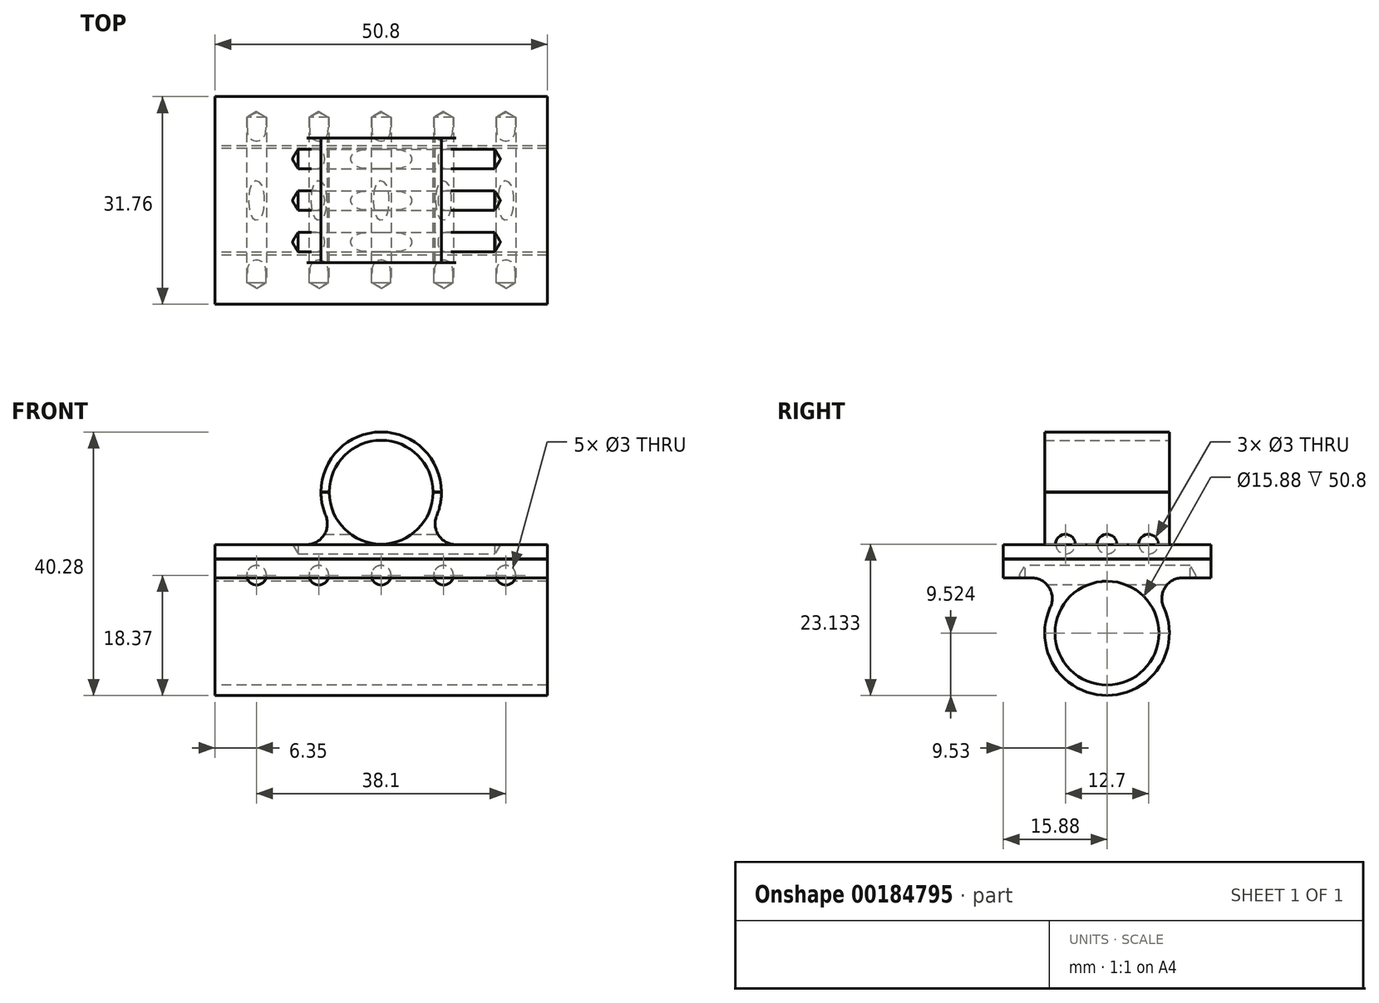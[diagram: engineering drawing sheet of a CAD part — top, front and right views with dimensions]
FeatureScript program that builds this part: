
annotation { "Feature Type Name" : "Feature", "Feature Type Description" : "" }
export const myFeature = defineFeature(function(context is Context, id is Id, definition is map)
    precondition{}
    {
        {
            var Q0;
            Q0=qCreatedBy(makeId("Front.planeOp"),FACE);
            var sketch = newSketch(context, id + "F0", { "sketchPlane" : qUnion([Q0])});
            skCircle(sketch, "E0", {"center": v(0, 0) * mm, "radius": 7.94 * mm});
            skArc(sketch, "E1", {"start": v(-7.54, -5.28) * mm, "mid": v(0, -9.2) * mm, "end": v(7.54, -5.28) * mm});
            skArc(sketch, "E2.trimOffspring", {"start": v(7.54, -5.28) * mm, "mid": v(0, 9.2) * mm, "end": v(-7.54, -5.28) * mm});
            skLineSegment(sketch, "E3", {"start": v(7.02, -4.92) * mm, "end": v(7.54, -5.28) * mm});
            skLineSegment(sketch, "E4", {"start": v(-7.02, -4.92) * mm, "end": v(-7.54, -5.28) * mm});
            skArc(sketch, "E5", {"start": v(-7.02, -4.92) * mm, "mid": v(0, -8.57) * mm, "end": v(7.02, -4.92) * mm});
            skSolve(sketch);
        }
        {
            var Q0;
            Q0 = qSketchRegion(id + "F0", true);
            extrude(context, id + "F1", {"entities" : qUnion([Q0]), "depth" : 9.52 * mm, "hasSecondDirection" : true, "secondDirectionOppositeDirection" : true, "secondDirectionDepth" : 9.52 * mm});
        }
        {
            var Q0;
            Q0=qCreatedBy(makeId("Front.planeOp"),FACE);
            var sketch = newSketch(context, id + "F2", { "sketchPlane" : qUnion([Q0])});
            skLineSegment(sketch, "E6.bottom", {"start": v(-25.4, 0.05) * mm, "end": v(25.4, 0.05) * mm});
            skLineSegment(sketch, "E6.top", {"start": v(-25.4, -0.05) * mm, "end": v(25.4, -0.05) * mm});
            skLineSegment(sketch, "E6.left", {"start": v(-25.4, 0.05) * mm, "end": v(-25.4, -0.05) * mm});
            skLineSegment(sketch, "E6.right", {"start": v(25.4, 0.05) * mm, "end": v(25.4, -0.05) * mm});
            skSolve(sketch);
        }
        {
            var Q0;
            Q0 = qSketchRegion(id + "F2", true);
            extrude(context, id + "F3", {"entities" : qUnion([Q0]), "operationType" : NewBodyOperationType.REMOVE, "oppositeDirection" : true, "depth" : 25.4 * mm, "hasSecondDirection" : true, "secondDirectionOppositeDirection" : false, "secondDirectionDepth" : 25.4 * mm});
        }
        {
            var Q0;
            Q0=qCreatedBy(makeId("Right.planeOp"),FACE);
            var sketch = newSketch(context, id + "F4", { "sketchPlane" : qUnion([Q0])});
            skCircle(sketch, "E7", {"center": v(0, -21.55) * mm, "radius": 7.94 * mm});
            skLineSegment(sketch, "E8.bottom", {"start": v(15.88, -8) * mm, "end": v(-15.88, -8) * mm});
            skLineSegment(sketch, "E8.top", {"start": v(15.88, -13.08) * mm, "end": v(11.55, -13.08) * mm});
            skLineSegment(sketch, "E8.left", {"start": v(15.88, -8) * mm, "end": v(15.88, -13.08) * mm});
            skLineSegment(sketch, "E8.right", {"start": v(-15.88, -8) * mm, "end": v(-15.88, -13.08) * mm});
            skArc(sketch, "E9", {"start": v(-8.66, -17.58) * mm, "mid": v(0, -31.07) * mm, "end": v(8.66, -17.58) * mm});
            skLineSegment(sketch, "E10", {"start": v(-11.55, -13.08) * mm, "end": v(-15.88, -13.08) * mm});
            skArc(sketch, "E11.filletArc", {"start": v(11.55, -13.08) * mm, "mid": v(8.87, -14.54) * mm, "end": v(8.66, -17.58) * mm});
            skArc(sketch, "E12.filletArc", {"start": v(-8.66, -17.58) * mm, "mid": v(-8.87, -14.54) * mm, "end": v(-11.55, -13.08) * mm});
            skSolve(sketch);
        }
        {
            var Q0;
            Q0 = qSketchRegion(id + "F4", true);
            extrude(context, id + "F5", {"entities" : qUnion([Q0]), "operationType" : NewBodyOperationType.ADD, "depth" : 25.4 * mm, "hasSecondDirection" : true, "secondDirectionOppositeDirection" : true, "secondDirectionDepth" : 25.4 * mm});
        }
        {
            var Q0;
            Q0=makeQuery(id+"F5.boolean.opBoolean","INTERSECT",EDGE,{"disambiguationData":[OD(0.0)],"derivedFrom":[makeQuery(id+"F1.opExtrude","SWEPT_FACE",FACE,{"disambiguationData":[OSD([sQuery(id+"F0.wireOp",EDGE,"E1")])]}),makeQuery(id+"F5.opExtrude","SWEPT_FACE",FACE,{"disambiguationData":[OSD([sQuery(id+"F4.wireOp",EDGE,"E8.bottom")])]})]});
            var Q1;
            Q1=makeQuery(id+"F5.boolean.opBoolean","INTERSECT",EDGE,{"disambiguationData":[OD(1.0)],"derivedFrom":[makeQuery(id+"F1.opExtrude","SWEPT_FACE",FACE,{"disambiguationData":[OSD([sQuery(id+"F0.wireOp",EDGE,"E1")])]}),makeQuery(id+"F5.opExtrude","SWEPT_FACE",FACE,{"disambiguationData":[OSD([sQuery(id+"F4.wireOp",EDGE,"E8.bottom")])]})]});
            fillet(context, id + "F6", {"entities" : qUnion([Q0, Q1]), "radius" : 3.17 * mm, "tangentPropagation" : true, "allowEdgeOverflow" : false});
        }
        {
            var Q0;
            Q0=qCreatedBy(makeId("Right.planeOp"),FACE);
            var sketch = newSketch(context, id + "F7", { "sketchPlane" : qUnion([Q0])});
            skLineSegment(sketch, "E13.bottom", {"start": v(-25.4, -10.16) * mm, "end": v(25.4, -10.16) * mm});
            skLineSegment(sketch, "E13.top", {"start": v(-25.4, -10.26) * mm, "end": v(25.4, -10.26) * mm});
            skLineSegment(sketch, "E13.left", {"start": v(-25.4, -10.16) * mm, "end": v(-25.4, -10.26) * mm});
            skLineSegment(sketch, "E13.right", {"start": v(25.4, -10.16) * mm, "end": v(25.4, -10.26) * mm});
            skSolve(sketch);
        }
        {
            var Q0;
            Q0 = qSketchRegion(id + "F7", true);
            extrude(context, id + "F8", {"entities" : qUnion([Q0]), "operationType" : NewBodyOperationType.REMOVE, "endBound" : BoundingType.THROUGH_ALL, "oppositeDirection" : true, "depth" : 50.8 * mm, "hasSecondDirection" : true, "secondDirectionBound" : SecondDirectionBoundingType.THROUGH_ALL, "secondDirectionOppositeDirection" : false, "secondDirectionDepth" : 50.8 * mm});
        }
        {
            var Q0;
            Q0=qCreatedBy(makeId("Right.planeOp"),FACE);
            var sketch = newSketch(context, id + "F9", { "sketchPlane" : qUnion([Q0])});
            skPoint(sketch, "E14", {"position": v(-6.35, -7.94) * mm});
            skPoint(sketch, "E15", {"position": v(6.35, -7.94) * mm});
            skPoint(sketch, "E16", {"position": v(0, -7.94) * mm});
            skSolve(sketch);
        }
        {
            var Q0;
            Q0=sQuery(id+"F9.wireOp",VERTEX,"E14");
            var Q1;
            Q1=sQuery(id+"F9.wireOp",VERTEX,"E16");
            var Q2;
            Q2=sQuery(id+"F9.wireOp",VERTEX,"E15");
            var Q3;
            Q3=makeQuery(id+"F8.boolean.opBoolean","SPLIT",BODY,{"disambiguationData":[OD(0.0)],"derivedFrom":makeQuery(id+"F3.boolean.opBoolean","SPLIT",BODY,{"disambiguationData":[OD(0.0)],"derivedFrom":makeQuery(id+"F1.opExtrude","SWEPT_BODY",BODY,{"disambiguationData":[OSD([sQuery(id+"F0.wireOp",EDGE,"E0"),sQuery(id+"F0.wireOp",EDGE,"E1"),sQuery(id+"F0.wireOp",EDGE,"E2.trimOffspring")])]})})});
            hole(context, id + "F10", {"style" : HoleStyle.SIMPLE, "endStyle" : HoleEndStyle.BLIND, "holeDiameter" : 3 * mm, "holeDepth" : 12.7 * mm, "locations" : qUnion([Q0, Q1, Q2]), "scope" : qUnion([Q3])});
        }
        {
            var Q0;
            Q0=sQuery(id+"F9.wireOp",VERTEX,"E14");
            var Q1;
            Q1=sQuery(id+"F9.wireOp",VERTEX,"E16");
            var Q2;
            Q2=sQuery(id+"F9.wireOp",VERTEX,"E15");
            var Q3;
            Q3=makeQuery(id+"F8.boolean.opBoolean","SPLIT",BODY,{"disambiguationData":[OD(0.0)],"derivedFrom":makeQuery(id+"F3.boolean.opBoolean","SPLIT",BODY,{"disambiguationData":[OD(0.0)],"derivedFrom":makeQuery(id+"F1.opExtrude","SWEPT_BODY",BODY,{"disambiguationData":[OSD([sQuery(id+"F0.wireOp",EDGE,"E0"),sQuery(id+"F0.wireOp",EDGE,"E1"),sQuery(id+"F0.wireOp",EDGE,"E2.trimOffspring")])]})})});
            hole(context, id + "F11", {"style" : HoleStyle.SIMPLE, "endStyle" : HoleEndStyle.BLIND, "oppositeDirection" : true, "holeDiameter" : 3 * mm, "holeDepth" : 12.7 * mm, "locations" : qUnion([Q0, Q1, Q2]), "scope" : qUnion([Q3])});
        }
        {
            var Q0;
            Q0=qCreatedBy(makeId("Front.planeOp"),FACE);
            var sketch = newSketch(context, id + "F12", { "sketchPlane" : qUnion([Q0])});
            skPoint(sketch, "E17", {"position": v(0, -12.7) * mm});
            skPoint(sketch, "E18", {"position": v(-9.53, -12.7) * mm});
            skPoint(sketch, "E19", {"position": v(-19.05, -12.7) * mm});
            skPoint(sketch, "E20", {"position": v(9.53, -12.7) * mm});
            skPoint(sketch, "E21", {"position": v(19.05, -12.7) * mm});
            skSolve(sketch);
        }
        {
            var Q0;
            Q0=sQuery(id+"F12.wireOp",VERTEX,"E19");
            var Q1;
            Q1=sQuery(id+"F12.wireOp",VERTEX,"E18");
            var Q2;
            Q2=sQuery(id+"F12.wireOp",VERTEX,"E17");
            var Q3;
            Q3=sQuery(id+"F12.wireOp",VERTEX,"E20");
            var Q4;
            Q4=sQuery(id+"F12.wireOp",VERTEX,"E21");
            var Q5;
            Q5=makeQuery(id+"F8.boolean.opBoolean","SPLIT",BODY,{"disambiguationData":[OD(1.0)],"derivedFrom":makeQuery(id+"F3.boolean.opBoolean","SPLIT",BODY,{"disambiguationData":[OD(0.0)],"derivedFrom":makeQuery(id+"F1.opExtrude","SWEPT_BODY",BODY,{"disambiguationData":[OSD([sQuery(id+"F0.wireOp",EDGE,"E0"),sQuery(id+"F0.wireOp",EDGE,"E1"),sQuery(id+"F0.wireOp",EDGE,"E2.trimOffspring")])]})})});
            hole(context, id + "F13", {"style" : HoleStyle.SIMPLE, "endStyle" : HoleEndStyle.BLIND, "holeDiameter" : 3 * mm, "holeDepth" : 12.7 * mm, "locations" : qUnion([Q0, Q1, Q2, Q3, Q4]), "scope" : qUnion([Q5])});
        }
        {
            var Q0;
            Q0=sQuery(id+"F12.wireOp",VERTEX,"E19");
            var Q1;
            Q1=sQuery(id+"F12.wireOp",VERTEX,"E18");
            var Q2;
            Q2=sQuery(id+"F12.wireOp",VERTEX,"E17");
            var Q3;
            Q3=sQuery(id+"F12.wireOp",VERTEX,"E20");
            var Q4;
            Q4=sQuery(id+"F12.wireOp",VERTEX,"E21");
            var Q5;
            Q5=makeQuery(id+"F8.boolean.opBoolean","SPLIT",BODY,{"disambiguationData":[OD(1.0)],"derivedFrom":makeQuery(id+"F3.boolean.opBoolean","SPLIT",BODY,{"disambiguationData":[OD(0.0)],"derivedFrom":makeQuery(id+"F1.opExtrude","SWEPT_BODY",BODY,{"disambiguationData":[OSD([sQuery(id+"F0.wireOp",EDGE,"E0"),sQuery(id+"F0.wireOp",EDGE,"E1"),sQuery(id+"F0.wireOp",EDGE,"E2.trimOffspring")])]})})});
            hole(context, id + "F14", {"style" : HoleStyle.SIMPLE, "endStyle" : HoleEndStyle.BLIND, "oppositeDirection" : true, "holeDiameter" : 3 * mm, "holeDepth" : 9.52 * mm, "locations" : qUnion([Q0, Q1, Q2, Q3, Q4]), "scope" : qUnion([Q5])});
        }
    });
